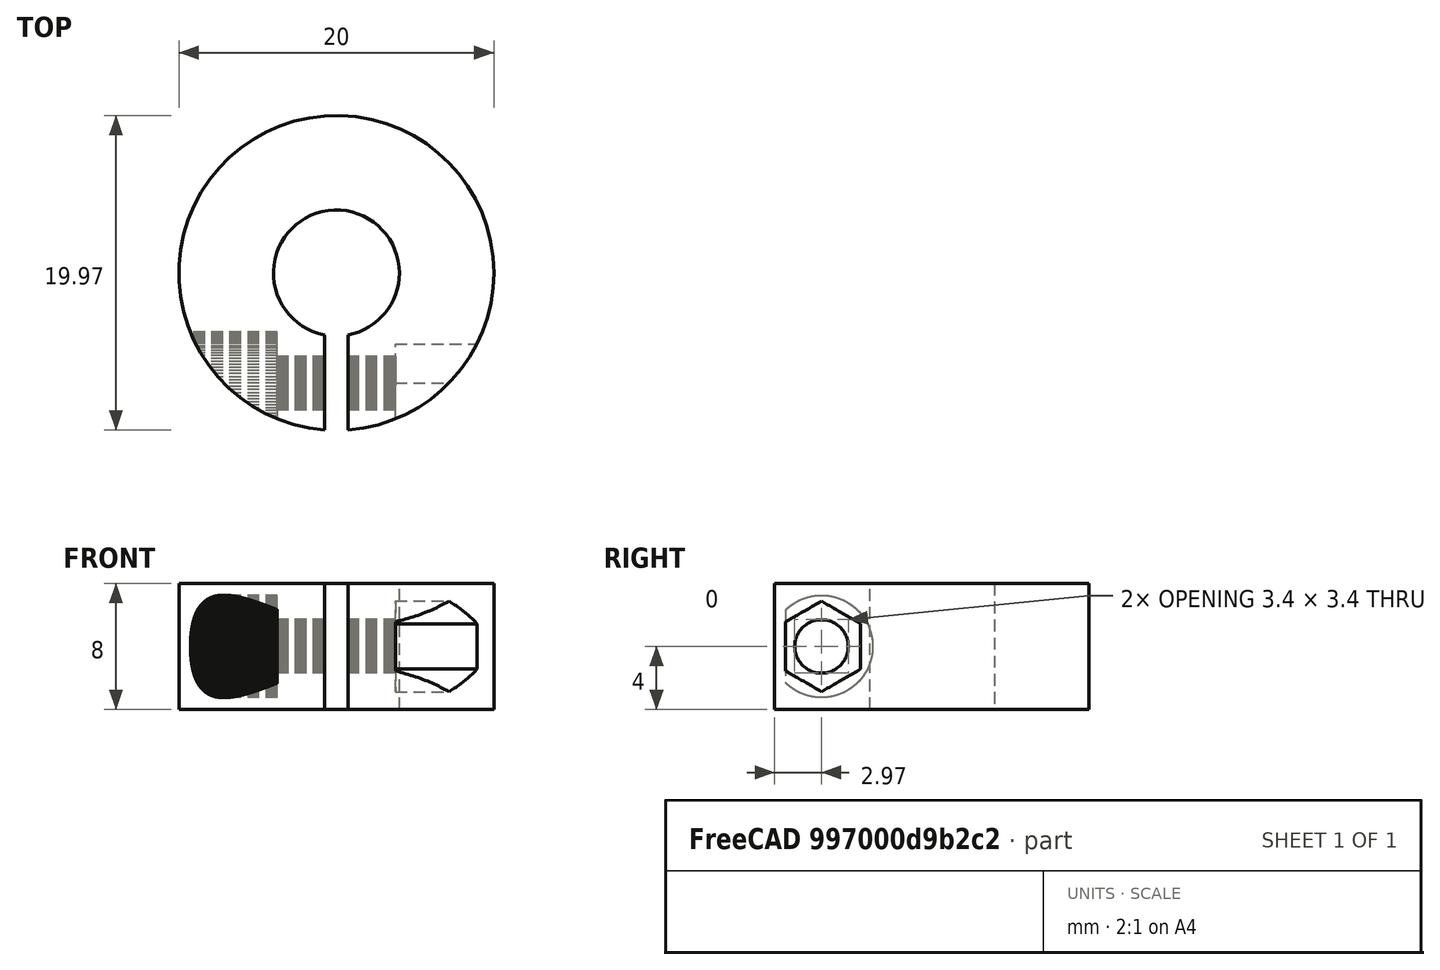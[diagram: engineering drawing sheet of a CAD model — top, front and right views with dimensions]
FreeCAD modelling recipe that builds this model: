
FCSTD DOCUMENT  (FreeCAD 0.18.3R)
Label: Parametric_Shaft_Collar
License: All rights reserved
LicenseURL: http://en.wikipedia.org/wiki/All_rights_reserved
objects: Part::Part2DObjectPython×4, Part::FeaturePython×4, Part::Extrusion×4, Part::Cut×2, Part::Plane×1, Part::Fuse×1, Part::Feature×1, Part::Mirroring×1, Part::MultiFuse×1
note: 19 computed .brp shape members not serialized (recipe doc carries the construction recipe); baked Part::Feature solids carry a one-line shape summary decoded from their .brp

FEATURE [Part::Part2DObjectPython] circle  # Draft 2D object (typed FeaturePython)
  FirstAngle = 0
  LastAngle = 0
  MakeFace = true
  Radius = 10
FEATURE [Part::Part2DObjectPython] circle001  # Draft 2D object (typed FeaturePython)
  FirstAngle = 0
  LastAngle = 0
  MakeFace = true
  Radius = 4
FEATURE [Part::Plane] square
  AttacherType = Attacher::AttachEngine3D
  Length = 1.5
  Placement = pos=(-0.75,-40,0) rot=(0,0,1;0rad)
  Width = 40
FEATURE [Part::Fuse] union
  Base = -> circle001
  Tool = -> square
FEATURE [Part::Cut] difference
  Base = -> circle
  Tool = -> union
FEATURE [Part::FeaturePython] RefineLinearExtrude  # WARN: FeaturePython — macro-defined, semantics opaque (R4)
  Base = -> difference
FEATURE [Part::Extrusion] LinearExtrude
  Base = -> RefineLinearExtrude
  Dir = (0,0,8)
  DirMode = 0
  FaceMakerClass = Part::FaceMakerBullseye
  LengthFwd = 0
  LengthRev = 0
  Solid = false
  Symmetric = false
FEATURE [Part::Part2DObjectPython] polygon  # Draft 2D object (typed FeaturePython)
  ChamferSize = 0
  DrawMode = 0
  FacesNumber = 100
  FilletRadius = 0
  MakeFace = true
  Radius = 1.7
FEATURE [Part::FeaturePython] RefineLinearExtrude001  # WARN: FeaturePython — macro-defined, semantics opaque (R4)
  Base = -> polygon
FEATURE [Part::Extrusion] LinearExtrude001
  Base = -> RefineLinearExtrude001
  Dir = (0,0,20)
  DirMode = 0
  FaceMakerClass = Part::FaceMakerBullseye
  LengthFwd = 0
  LengthRev = 0
  Placement = pos=(0,0,-10) rot=(0,0,1;0rad)
  Solid = false
  Symmetric = false
FEATURE [Part::Part2DObjectPython] polygon001  # Draft 2D object (typed FeaturePython)
  ChamferSize = 0
  DrawMode = 0
  FacesNumber = 100
  FilletRadius = 0
  MakeFace = true
  Radius = 3.25
FEATURE [Part::FeaturePython] RefineLinearExtrude002  # WARN: FeaturePython — macro-defined, semantics opaque (R4)
  Base = -> polygon001
FEATURE [Part::Extrusion] LinearExtrude002
  Base = -> RefineLinearExtrude002
  Dir = (0,0,20)
  DirMode = 0
  FaceMakerClass = Part::FaceMakerBullseye
  LengthFwd = 0
  LengthRev = 0
  Placement = pos=(0,0,3.75) rot=(0,0,1;0rad)
  Solid = false
  Symmetric = false
FEATURE [Part::Feature] polygon002
  shape: bbox 5.75 x 4.98 x 2e-07 mm, 1 faces, 0 solids (baked)
FEATURE [Part::FeaturePython] RefineLinearExtrude003  # WARN: FeaturePython — macro-defined, semantics opaque (R4)
  Base = -> polygon002
FEATURE [Part::Extrusion] LinearExtrude003
  Base = -> RefineLinearExtrude003
  Dir = (0,0,20)
  DirMode = 0
  FaceMakerClass = Part::FaceMakerBullseye
  LengthFwd = 0
  LengthRev = 0
  Placement = pos=(0,0,3.75) rot=(0,0,1;0rad)
  Solid = false
  Symmetric = false
FEATURE [Part::Mirroring] mirr_LinearExtrude003  label="mirrored LinearExtrude003"
  Base = (0,0,0)
  Normal = (0,0,1)
  Source = -> LinearExtrude003
FEATURE [Part::MultiFuse] union001
  Placement = pos=(0,-7,4) rot=(0.707107,0,-0.707107;3.14159rad)
  Shapes = -> [LinearExtrude001,LinearExtrude002,mirr_LinearExtrude003]
FEATURE [Part::Cut] difference001
  Base = -> LinearExtrude
  Tool = -> union001
